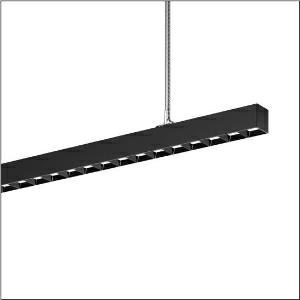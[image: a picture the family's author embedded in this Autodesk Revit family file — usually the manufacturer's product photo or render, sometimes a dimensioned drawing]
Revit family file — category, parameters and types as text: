
# Revit family: silica_r__21_51mx31dc4dbb_76cd
name_source: partatom
category: Lighting Fixtures
units: mm (PartAtom-declared; Revit-internal decimal feet)

## family parameters
Cut with Voids When Loaded = No
Host = Face
Light Source = No
Part Type = Normal
Room Calculation Point = No
Round Connector Dimension = Use Diameter
Shared = No

## types (1)
- --- (1 x LED, 18230 lm, 105.9 W, 4000K)
    Apparent Load = 106 VA
    CIE Flux Codes = 87 99 100 59 100
    Color Rendering = 80
    Color Temperature = 4000K
    Default Elevation = 1800 mm
    Description = Silica® 21, office luminaire, primary light control with darklight reflector, of PMMA, black, CAT 2 (L<= 3000cd/m²), light emission: direct/indirect distribution, primary light characteristic: symmetric, installation type: suspended mounting, LED, rated luminous flux: 18.230lm, luminous efficacy: 172lm/W, light colour: 840, colour temperature: 4000K, with terminal, 3+2-pole, max. 2.5mm², mains connection: 220..240V, AC, 50/60Hz, rated input power: 105.9W, luminaire housing, of aluminium, jet black (RAL 9005), length: 3.004mm, width: 53mm, height: 53mm, protection rating (complete): IP20, insulation class (complete): insulation class I (protective earthing), certification: CE, permissible operating ambient temperature: 0..+35°C, standard: EN 50419, packaging unit: 1 piece
    Height = 53 mm
    Lamp = 1 x LED
    Lamp Light Flux = 18230 lm
    Lamp Power = 105.9 W
    Lamp count = 1
    Length = 3004 mm
    Luminous efficacy = 172 lm/W
    Manufacturer = Siteco
    ModVariant = No
    Model = 51MX31DC4DBB
    Mounting Place = Ceiling
    Mounting Type = Pendant
    Number of Poles = 1
    OnlyDefault = Yes
    Power Factor = 1
    Product Name = Silica® 21
    Product group = office luminaire | ceiling pendant
    ProductGroupID = 902
    Protection Class = Protection class I
    Protection Degree = IP 20
    RLX_Detail_Level = 1
    RLX_Emergency_Light_Flux = 0 lm
    RLX_Emergency_Type = 0
    RLX_Emergency_Type_DB = No
    RlxData = <blob elided: 66873 chars, md5=b510e53c>
    Socket = socket
    Standby Power = 0 W
    System Light Flux = 18230 lm
    System Power = 106 W
    Type Comments = factory setting: luminous flux: 100 % | dim-lin: 254 | 367 mA
    Type Image = l_1297774.jpg
    URL = http://relux.com
    VarID = @adj_051797
    Voltage = 0 V
    Weight = 0.00 kg
    Width = 53 mm

## geometry (parser evidence)
native form markers: Blend x4, Sweep x11
no freeform markers — native parametric forms only
